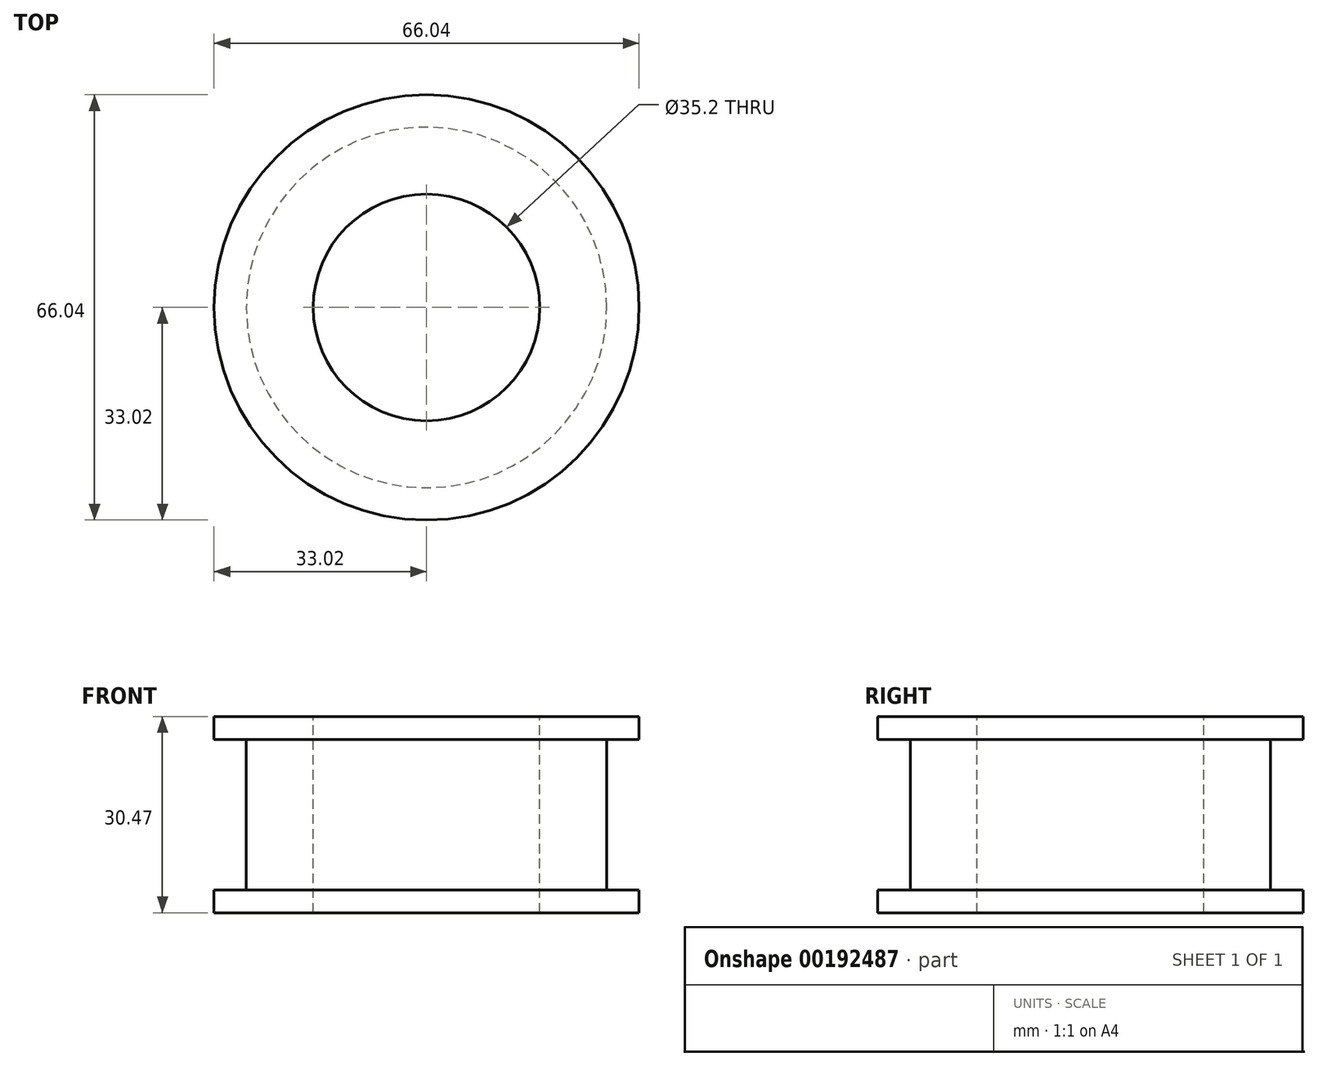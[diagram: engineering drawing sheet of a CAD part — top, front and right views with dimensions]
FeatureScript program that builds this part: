
annotation { "Feature Type Name" : "Feature", "Feature Type Description" : "" }
export const myFeature = defineFeature(function(context is Context, id is Id, definition is map)
    precondition{}
    {
        {
            var Q0;
            Q0=qCreatedBy(makeId("Top.planeOp"),FACE);
            var sketch = newSketch(context, id + "F0", { "sketchPlane" : qUnion([Q0])});
            skCircle(sketch, "E0", {"center": v(0, 0) * mm, "radius": 33.02 * mm});
            skSolve(sketch);
        }
        {
            var Q0;
            Q0 = qSketchRegion(id + "F0", true);
            extrude(context, id + "F1", {"entities" : qUnion([Q0]), "depth" : 3.55 * mm});
        }
        {
            var Q0;
            Q0=makeQuery(id+"F1.opExtrude","CAP_FACE",FACE,{"disambiguationData":[OSD([sQuery(id+"F0.wireOp",EDGE,"E0")])],"isStart":false});
            var sketch = newSketch(context, id + "F2", { "sketchPlane" : qUnion([Q0])});
            skCircle(sketch, "E1", {"center": v(0, 0) * mm, "radius": 28 * mm});
            skSolve(sketch);
        }
        {
            var Q0;
            Q0 = qSketchRegion(id + "F2", true);
            extrude(context, id + "F3", {"entities" : qUnion([Q0]), "operationType" : NewBodyOperationType.ADD, "depth" : 23.37 * mm});
        }
        {
            var Q0;
            Q0=makeQuery(id+"F3.opExtrude","CAP_FACE",FACE,{"disambiguationData":[OSD([sQuery(id+"F2.wireOp",EDGE,"E1")])],"isStart":false});
            var sketch = newSketch(context, id + "F4", { "sketchPlane" : qUnion([Q0])});
            skCircle(sketch, "E2.0", {"center": v(0, 0) * mm, "radius": 33.02 * mm});
            skSolve(sketch);
        }
        {
            var Q0;
            Q0 = qSketchRegion(id + "F4", true);
            extrude(context, id + "F5", {"entities" : qUnion([Q0]), "operationType" : NewBodyOperationType.ADD, "depth" : 3.55 * mm});
        }
        {
            var Q0;
            Q0=makeQuery(id+"F5.opExtrude","CAP_FACE",FACE,{"disambiguationData":[OSD([sQuery(id+"F4.wireOp",EDGE,"E2.0")])],"isStart":false});
            var sketch = newSketch(context, id + "F6", { "sketchPlane" : qUnion([Q0])});
            skCircle(sketch, "E3", {"center": v(0, 0) * mm, "radius": 17.6 * mm});
            skSolve(sketch);
        }
        {
            var Q0;
            Q0 = qSketchRegion(id + "F6", true);
            extrude(context, id + "F7", {"entities" : qUnion([Q0]), "operationType" : NewBodyOperationType.REMOVE, "endBound" : BoundingType.THROUGH_ALL, "oppositeDirection" : true, "depth" : 25.4 * mm});
        }
    });
